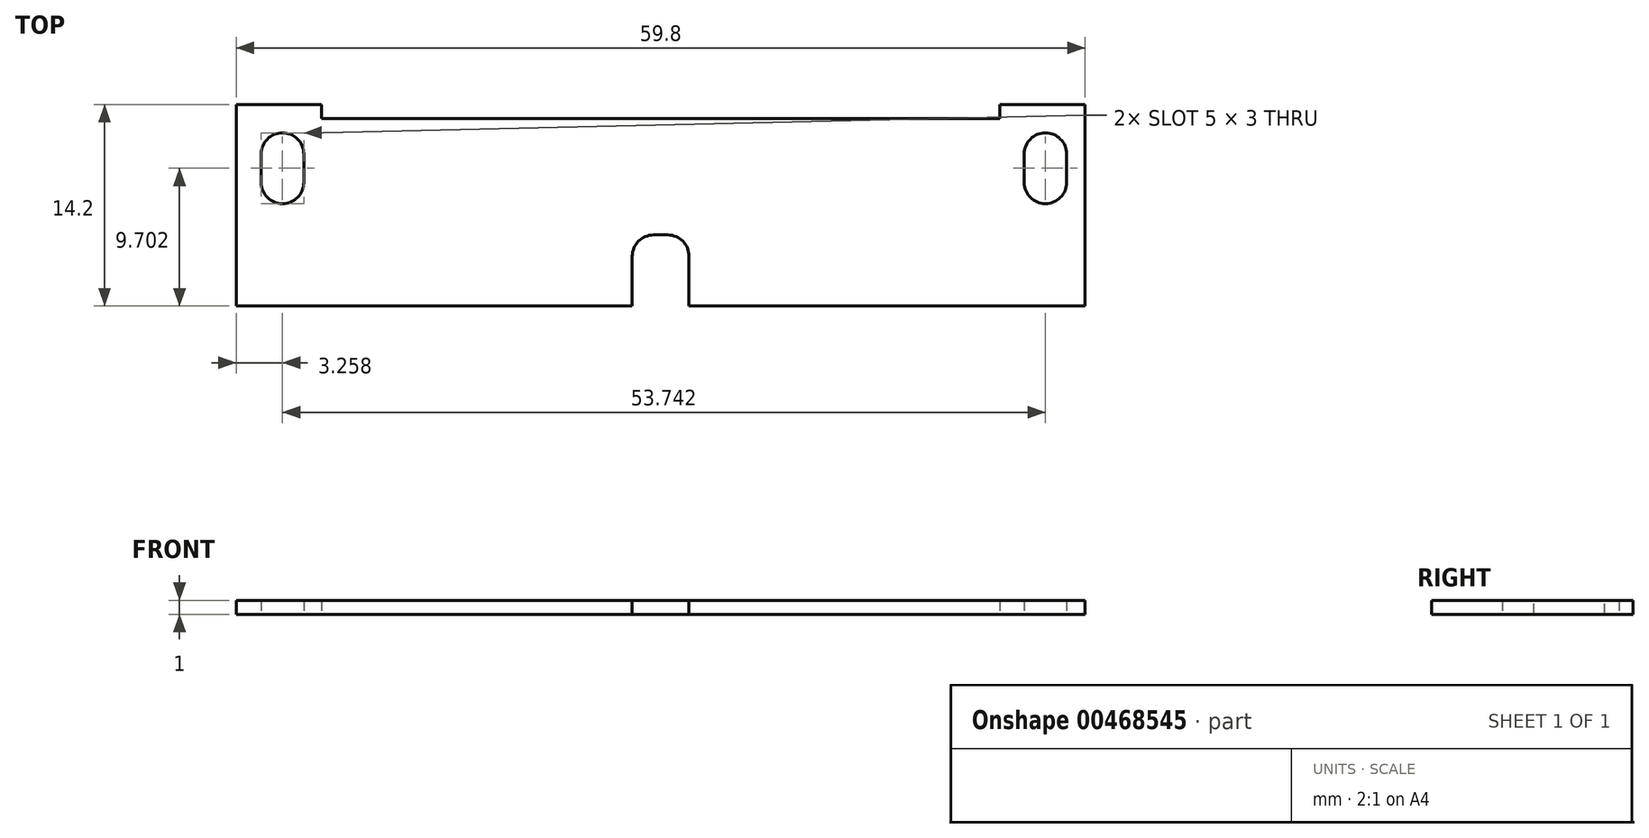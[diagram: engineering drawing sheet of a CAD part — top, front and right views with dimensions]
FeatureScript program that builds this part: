
annotation { "Feature Type Name" : "Feature", "Feature Type Description" : "" }
export const myFeature = defineFeature(function(context is Context, id is Id, definition is map)
    precondition{}
    {
        {
            var Q0;
            Q0=qCreatedBy(makeId("Top.planeOp"),FACE);
            var sketch = newSketch(context, id + "F0", { "sketchPlane" : qUnion([Q0])});
            skLineSegment(sketch, "E0.bottom", {"start": v(-19.6, 6.54) * mm, "end": v(40.2, 6.54) * mm});
            skLineSegment(sketch, "E0.top", {"start": v(-19.6, -7.66) * mm, "end": v(8.3, -7.66) * mm});
            skLineSegment(sketch, "E0.left", {"start": v(-19.6, 6.54) * mm, "end": v(-19.6, -7.66) * mm});
            skLineSegment(sketch, "E0.right", {"start": v(40.2, 6.54) * mm, "end": v(40.2, -7.66) * mm});
            skPoint(sketch, "E1", {"position": v(8.3, -7.66) * mm});
            skPoint(sketch, "E2", {"position": v(12.3, -7.66) * mm});
            skLineSegment(sketch, "E3.trimOffspring", {"start": v(12.3, -7.66) * mm, "end": v(40.2, -7.66) * mm});
            skLineSegment(sketch, "E4.bottom", {"start": v(-17.83, 4.54) * mm, "end": v(-14.83, 4.54) * mm});
            skLineSegment(sketch, "E4.top", {"start": v(-17.83, -0.46) * mm, "end": v(-14.83, -0.46) * mm});
            skLineSegment(sketch, "E4.left", {"start": v(-17.83, 4.54) * mm, "end": v(-17.83, -0.46) * mm});
            skLineSegment(sketch, "E4.right", {"start": v(-14.83, 4.54) * mm, "end": v(-14.83, -0.46) * mm});
            skLineSegment(sketch, "E5.bottom", {"start": v(35.91, 4.54) * mm, "end": v(38.91, 4.54) * mm});
            skLineSegment(sketch, "E5.top", {"start": v(35.91, -0.46) * mm, "end": v(38.91, -0.46) * mm});
            skLineSegment(sketch, "E5.left", {"start": v(35.91, 4.54) * mm, "end": v(35.91, -0.46) * mm});
            skLineSegment(sketch, "E5.right", {"start": v(38.91, 4.54) * mm, "end": v(38.91, -0.46) * mm});
            skLineSegment(sketch, "E6", {"start": v(8.3, -7.66) * mm, "end": v(12.3, -7.66) * mm});
            skLineSegment(sketch, "E7.top", {"start": v(8.3, -2.66) * mm, "end": v(12.3, -2.66) * mm});
            skLineSegment(sketch, "E7.left", {"start": v(8.3, -7.66) * mm, "end": v(8.3, -2.66) * mm});
            skLineSegment(sketch, "E7.right", {"start": v(12.3, -7.66) * mm, "end": v(12.3, -2.66) * mm});
            skLineSegment(sketch, "E8", {"start": v(-13.6, 6.54) * mm, "end": v(-13.6, 5.54) * mm});
            skLineSegment(sketch, "E9", {"start": v(-13.6, 5.54) * mm, "end": v(34.2, 5.54) * mm});
            skLineSegment(sketch, "E10", {"start": v(34.2, 5.54) * mm, "end": v(34.2, 6.54) * mm});
            skSolve(sketch);
        }
        {
            var Q0;
            Q0=makeQuery(id+"F0.imprint","IMPRINT",FACE,{"disambiguationData":[TD([[makeQuery(id+"F0.imprint","IMPRINT",EDGE,{"derivedFrom":sQuery(id+"F0.wireOp",EDGE,"E0.bottom")}),-1.0]])]});
            extrude(context, id + "F1", {"entities" : qUnion([Q0]), "depth" : 1 * mm, "offsetDistance" : 25 * mm});
        }
        {
            var Q0;
            Q0=makeQuery(id+"F1.opExtrude","SWEPT_EDGE",EDGE,{"disambiguationData":[OSD([sQuery(id+"F0.wireOp",EDGE,"E4.bottom"),sQuery(id+"F0.wireOp",EDGE,"E4.left")])]});
            var Q1;
            Q1=makeQuery(id+"F1.opExtrude","SWEPT_EDGE",EDGE,{"disambiguationData":[OSD([sQuery(id+"F0.wireOp",EDGE,"E4.bottom"),sQuery(id+"F0.wireOp",EDGE,"E4.right")])]});
            var Q2;
            Q2=makeQuery(id+"F1.opExtrude","SWEPT_EDGE",EDGE,{"disambiguationData":[OSD([sQuery(id+"F0.wireOp",EDGE,"E4.top"),sQuery(id+"F0.wireOp",EDGE,"E4.right")])]});
            var Q3;
            Q3=makeQuery(id+"F1.opExtrude","SWEPT_EDGE",EDGE,{"disambiguationData":[OSD([sQuery(id+"F0.wireOp",EDGE,"E4.top"),sQuery(id+"F0.wireOp",EDGE,"E4.left")])]});
            var Q4;
            Q4=makeQuery(id+"F1.opExtrude","SWEPT_EDGE",EDGE,{"disambiguationData":[OSD([sQuery(id+"F0.wireOp",EDGE,"E5.bottom"),sQuery(id+"F0.wireOp",EDGE,"E5.right")])]});
            var Q5;
            Q5=makeQuery(id+"F1.opExtrude","SWEPT_EDGE",EDGE,{"disambiguationData":[OSD([sQuery(id+"F0.wireOp",EDGE,"E5.bottom"),sQuery(id+"F0.wireOp",EDGE,"E5.left")])]});
            var Q6;
            Q6=makeQuery(id+"F1.opExtrude","SWEPT_EDGE",EDGE,{"disambiguationData":[OSD([sQuery(id+"F0.wireOp",EDGE,"E5.top"),sQuery(id+"F0.wireOp",EDGE,"E5.left")])]});
            var Q7;
            Q7=makeQuery(id+"F1.opExtrude","SWEPT_EDGE",EDGE,{"disambiguationData":[OSD([sQuery(id+"F0.wireOp",EDGE,"E5.top"),sQuery(id+"F0.wireOp",EDGE,"E5.right")])]});
            fillet(context, id + "F2", {"entities" : qUnion([Q0, Q1, Q2, Q3, Q4, Q5, Q6, Q7]), "tangentPropagation" : true, "radius" : 1.5 * mm, "defaultsChanged" : false, "vertexSettings" : [], "allowEdgeOverflow" : false});
        }
        {
            var Q0;
            Q0=makeQuery(id+"F1.opExtrude","SWEPT_EDGE",EDGE,{"disambiguationData":[OSD([sQuery(id+"F0.wireOp",EDGE,"E7.top"),sQuery(id+"F0.wireOp",EDGE,"E7.left")])]});
            var Q1;
            Q1=makeQuery(id+"F1.opExtrude","SWEPT_EDGE",EDGE,{"disambiguationData":[OSD([sQuery(id+"F0.wireOp",EDGE,"E7.top"),sQuery(id+"F0.wireOp",EDGE,"E7.right")])]});
            fillet(context, id + "F3", {"entities" : qUnion([Q0, Q1]), "tangentPropagation" : true, "radius" : 1.5 * mm, "defaultsChanged" : false, "vertexSettings" : [], "allowEdgeOverflow" : false});
        }
    });
